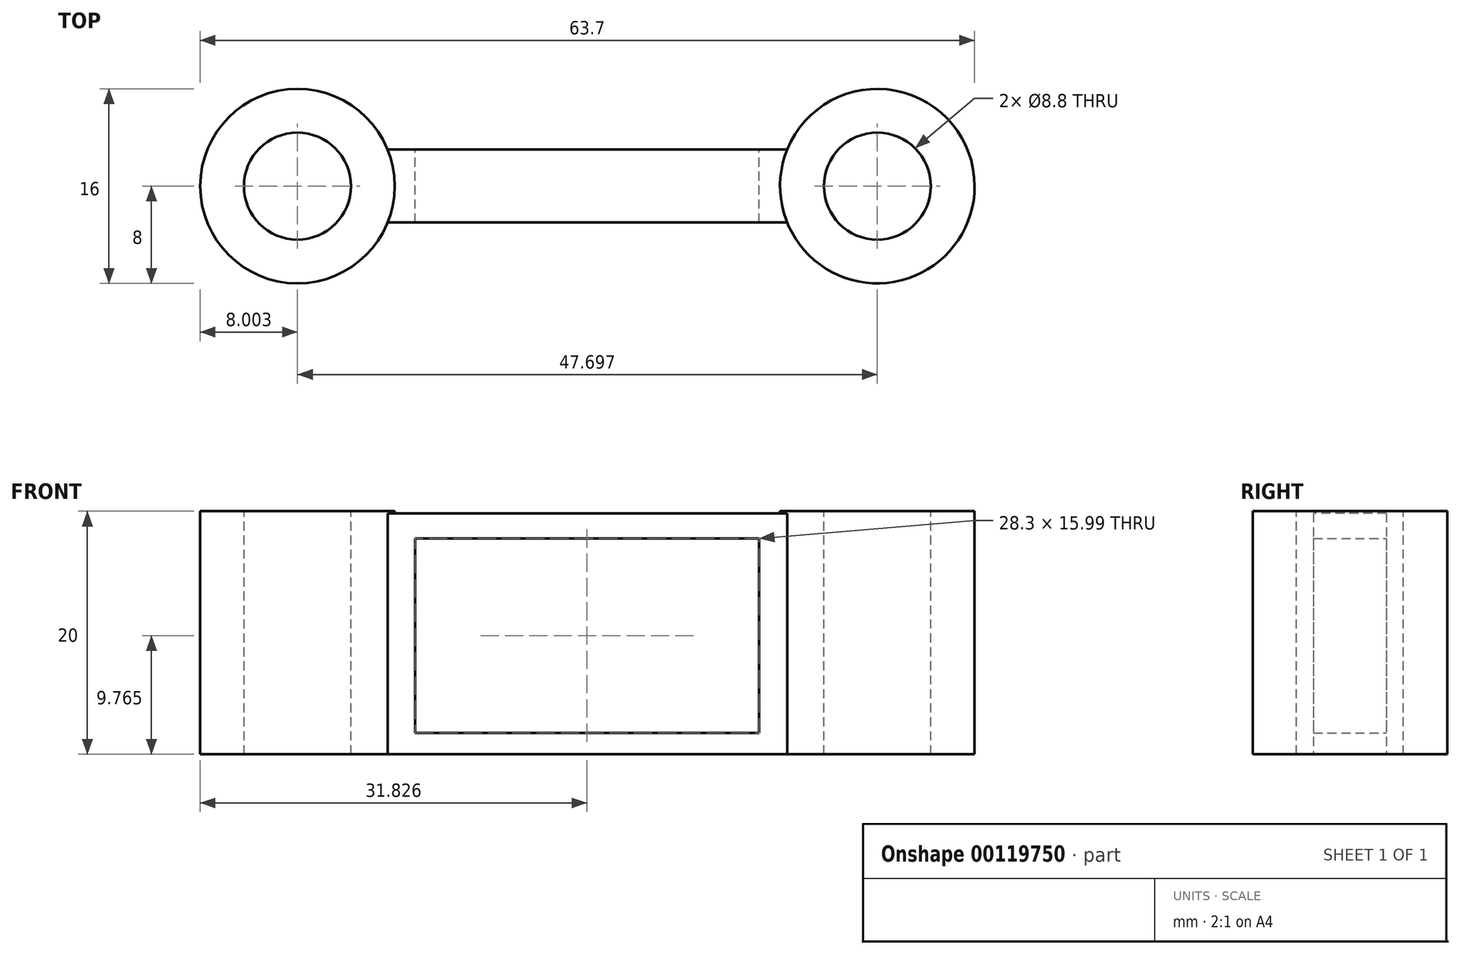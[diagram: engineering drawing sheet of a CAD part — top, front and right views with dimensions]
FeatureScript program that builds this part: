
annotation { "Feature Type Name" : "Feature", "Feature Type Description" : "" }
export const myFeature = defineFeature(function(context is Context, id is Id, definition is map)
    precondition{}
    {
        {
            var Q0;
            Q0=qCreatedBy(makeId("Top.planeOp"),FACE);
            var sketch = newSketch(context, id + "F0", { "sketchPlane" : qUnion([Q0])});
            skCircle(sketch, "E0", {"center": v(0, 0) * mm, "radius": 8 * mm});
            skSolve(sketch);
        }
        {
            var Q0;
            Q0 = qSketchRegion(id + "F0", true);
            extrude(context, id + "F1", {"entities" : qUnion([Q0]), "depth" : 20 * mm});
        }
        {
            var Q0;
            Q0=makeQuery(id+"F1.opExtrude","CAP_FACE",FACE,{"disambiguationData":[OSD([sQuery(id+"F0.wireOp",EDGE,"E0")])],"isStart":false});
            var sketch = newSketch(context, id + "F2", { "sketchPlane" : qUnion([Q0])});
            skCircle(sketch, "E1", {"center": v(0, 0) * mm, "radius": 4.4 * mm});
            skSolve(sketch);
        }
        {
            var Q0;
            Q0 = qSketchRegion(id + "F2", true);
            extrude(context, id + "F3", {"entities" : qUnion([Q0]), "operationType" : NewBodyOperationType.REMOVE, "oppositeDirection" : true, "depth" : 20 * mm});
        }
        {
            var Q0;
            Q0=qCreatedBy(makeId("Front.planeOp"),FACE);
            var sketch = newSketch(context, id + "F4", { "sketchPlane" : qUnion([Q0])});
            skLineSegment(sketch, "E2", {"start": v(-6.47, 0) * mm, "end": v(-40.56, 0) * mm});
            skLineSegment(sketch, "E3", {"start": v(-40.56, 0) * mm, "end": v(-40.56, 19.83) * mm});
            skLineSegment(sketch, "E4", {"start": v(-6.47, 19.83) * mm, "end": v(-6.47, 0) * mm});
            skLineSegment(sketch, "E5", {"start": v(-40.56, 19.83) * mm, "end": v(-6.47, 19.83) * mm});
            skLineSegment(sketch, "E6.bottom", {"start": v(-38.02, 17.76) * mm, "end": v(-9.72, 17.76) * mm});
            skLineSegment(sketch, "E6.top", {"start": v(-38.02, 1.77) * mm, "end": v(-9.72, 1.77) * mm});
            skLineSegment(sketch, "E6.left", {"start": v(-38.02, 17.76) * mm, "end": v(-38.02, 1.77) * mm});
            skLineSegment(sketch, "E6.right", {"start": v(-9.72, 17.76) * mm, "end": v(-9.72, 1.77) * mm});
            skSolve(sketch);
        }
        {
            var Q0;
            Q0 = qSketchRegion(id + "F4", true);
            extrude(context, id + "F5", {"entities" : qUnion([Q0]), "operationType" : NewBodyOperationType.ADD, "depth" : 3 * mm});
        }
        {
            var Q0;
            Q0 = qSketchRegion(id + "F4", true);
            extrude(context, id + "F6", {"entities" : qUnion([Q0]), "operationType" : NewBodyOperationType.ADD, "oppositeDirection" : true, "depth" : 3 * mm});
        }
        {
            var Q0;
            {var subQ0=sQuery(id+"F4.wireOp",EDGE,"E2");Q0=makeQuery(id+"F6.boolean.opBoolean","MERGE",FACE,{"derivedFrom":[makeQuery(id+"F5.boolean.opBoolean","MERGE",FACE,{"derivedFrom":[makeQuery(id+"F1.opExtrude","CAP_FACE",FACE,{"disambiguationData":[OSD([sQuery(id+"F0.wireOp",EDGE,"E0")])],"isStart":true}),makeQuery(id+"F5.opExtrude","SWEPT_FACE",FACE,{"disambiguationData":[OSD([subQ0])]})]}),makeQuery(id+"F6.opExtrude","SWEPT_FACE",FACE,{"disambiguationData":[OSD([subQ0])]})]});}
            var sketch = newSketch(context, id + "F7", { "sketchPlane" : qUnion([Q0])});
            skCircle(sketch, "E7", {"center": v(-47.7, 0) * mm, "radius": 8 * mm});
            skSolve(sketch);
        }
        {
            var Q0;
            Q0 = qSketchRegion(id + "F7", true);
            extrude(context, id + "F8", {"entities" : qUnion([Q0]), "operationType" : NewBodyOperationType.ADD, "oppositeDirection" : true, "depth" : 20 * mm});
        }
        {
            var Q0;
            Q0=makeQuery(id+"F8.opExtrude","CAP_FACE",FACE,{"disambiguationData":[OSD([sQuery(id+"F7.wireOp",EDGE,"E7")])],"isStart":false});
            var sketch = newSketch(context, id + "F9", { "sketchPlane" : qUnion([Q0])});
            skCircle(sketch, "E8", {"center": v(-47.7, 0) * mm, "radius": 4.4 * mm});
            skSolve(sketch);
        }
        {
            var Q0;
            Q0 = qSketchRegion(id + "F9", true);
            extrude(context, id + "F10", {"entities" : qUnion([Q0]), "operationType" : NewBodyOperationType.REMOVE, "oppositeDirection" : true, "depth" : 20 * mm});
        }
    });
